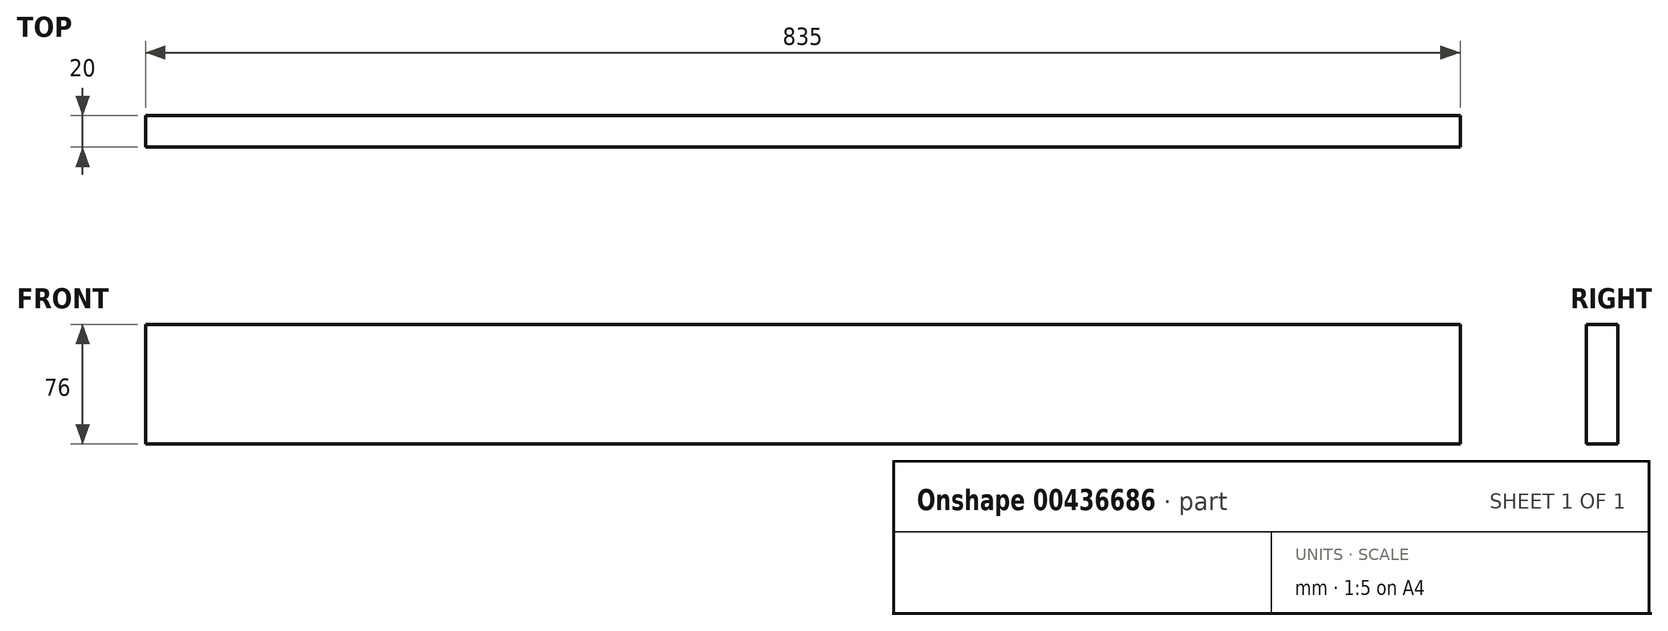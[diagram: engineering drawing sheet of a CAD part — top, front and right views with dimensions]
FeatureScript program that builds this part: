
annotation { "Feature Type Name" : "Feature", "Feature Type Description" : "" }
export const myFeature = defineFeature(function(context is Context, id is Id, definition is map)
    precondition{}
    {
        {
            var Q0;
            Q0=qCreatedBy(makeId("Right.planeOp"),FACE);
            var sketch = newSketch(context, id + "F0", { "sketchPlane" : qUnion([Q0])});
            skLineSegment(sketch, "E0.bottom", {"start": v(10, 38) * mm, "end": v(-10, 38) * mm});
            skLineSegment(sketch, "E0.top", {"start": v(10, -38) * mm, "end": v(-10, -38) * mm});
            skLineSegment(sketch, "E0.left", {"start": v(10, 38) * mm, "end": v(10, -38) * mm});
            skLineSegment(sketch, "E0.right", {"start": v(-10, 38) * mm, "end": v(-10, -38) * mm});
            skPoint(sketch, "E0.middle", {"position": v(0, 0) * mm});
            skSolve(sketch);
        }
        {
            var Q0;
            Q0 = qSketchRegion(id + "F0", true);
            extrude(context, id + "F1", {"entities" : qUnion([Q0]), "depth" : 835 * mm});
        }
    });
